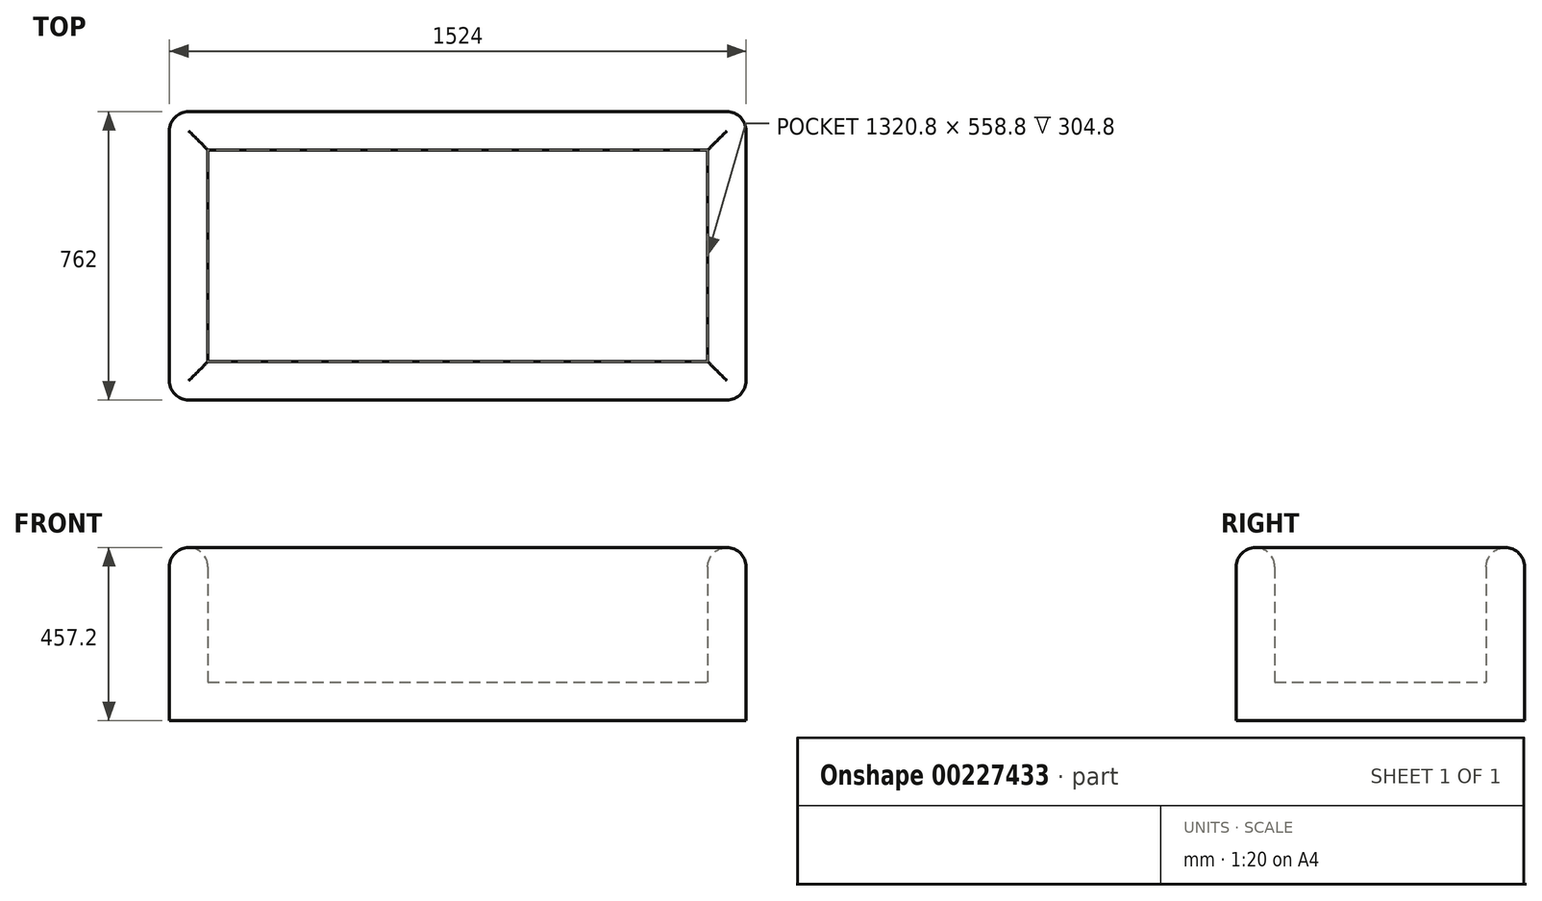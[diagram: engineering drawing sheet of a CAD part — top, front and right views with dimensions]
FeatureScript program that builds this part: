
annotation { "Feature Type Name" : "Feature", "Feature Type Description" : "" }
export const myFeature = defineFeature(function(context is Context, id is Id, definition is map)
    precondition{}
    {
        {
            var Q0;
            Q0=qCreatedBy(makeId("Top.planeOp"),FACE);
            var sketch = newSketch(context, id + "F0", { "sketchPlane" : qUnion([Q0])});
            skLineSegment(sketch, "E0.bottom", {"start": v(0, 0) * mm, "end": v(1524, 0) * mm});
            skLineSegment(sketch, "E0.top", {"start": v(0, 762) * mm, "end": v(1524, 762) * mm});
            skLineSegment(sketch, "E0.left", {"start": v(0, 0) * mm, "end": v(0, 762) * mm});
            skLineSegment(sketch, "E0.right", {"start": v(1524, 0) * mm, "end": v(1524, 762) * mm});
            skSolve(sketch);
        }
        {
            var Q0;
            Q0=makeQuery(id+"F0.imprint","IMPRINT",FACE,{"disambiguationData":[TD([[makeQuery(id+"F0.imprint","IMPRINT",EDGE,{"derivedFrom":sQuery(id+"F0.wireOp",EDGE,"E0.bottom")}),1.0]])]});
            extrude(context, id + "F1", {"entities" : qUnion([Q0]), "depth" : 457.2 * mm});
        }
        {
            var Q0;
            Q0=makeQuery(id+"F1.opExtrude","CAP_FACE",FACE,{"disambiguationData":[OSD([sQuery(id+"F0.wireOp",EDGE,"E0.bottom"),sQuery(id+"F0.wireOp",EDGE,"E0.top"),sQuery(id+"F0.wireOp",EDGE,"E0.left"),sQuery(id+"F0.wireOp",EDGE,"E0.right")])],"isStart":false});
            shell(context, id + "F2", {"entities" : qUnion([Q0]), "thickness" : 101.6 * mm});
        }
        {
            var Q0;
            Q0=makeQuery(id+"F1.opExtrude","CAP_FACE",FACE,{"disambiguationData":[OSD([sQuery(id+"F0.wireOp",EDGE,"E0.bottom"),sQuery(id+"F0.wireOp",EDGE,"E0.top"),sQuery(id+"F0.wireOp",EDGE,"E0.left"),sQuery(id+"F0.wireOp",EDGE,"E0.right")])],"isStart":false});
            var Q1;
            Q1=makeQuery(id+"F1.opExtrude","SWEPT_EDGE",EDGE,{"disambiguationData":[OSD([sQuery(id+"F0.wireOp",EDGE,"E0.top"),sQuery(id+"F0.wireOp",EDGE,"E0.right")])]});
            var Q2;
            Q2=makeQuery(id+"F1.opExtrude","SWEPT_EDGE",EDGE,{"disambiguationData":[OSD([sQuery(id+"F0.wireOp",EDGE,"E0.top"),sQuery(id+"F0.wireOp",EDGE,"E0.left")])]});
            var Q3;
            Q3=makeQuery(id+"F1.opExtrude","SWEPT_EDGE",EDGE,{"disambiguationData":[OSD([sQuery(id+"F0.wireOp",EDGE,"E0.bottom"),sQuery(id+"F0.wireOp",EDGE,"E0.left")])]});
            var Q4;
            Q4=makeQuery(id+"F1.opExtrude","SWEPT_EDGE",EDGE,{"disambiguationData":[OSD([sQuery(id+"F0.wireOp",EDGE,"E0.bottom"),sQuery(id+"F0.wireOp",EDGE,"E0.right")])]});
            fillet(context, id + "F3", {"entities" : qUnion([Q0, Q1, Q2, Q3, Q4]), "radius" : 50.8 * mm, "tangentPropagation" : true, "allowEdgeOverflow" : false});
        }
    });
